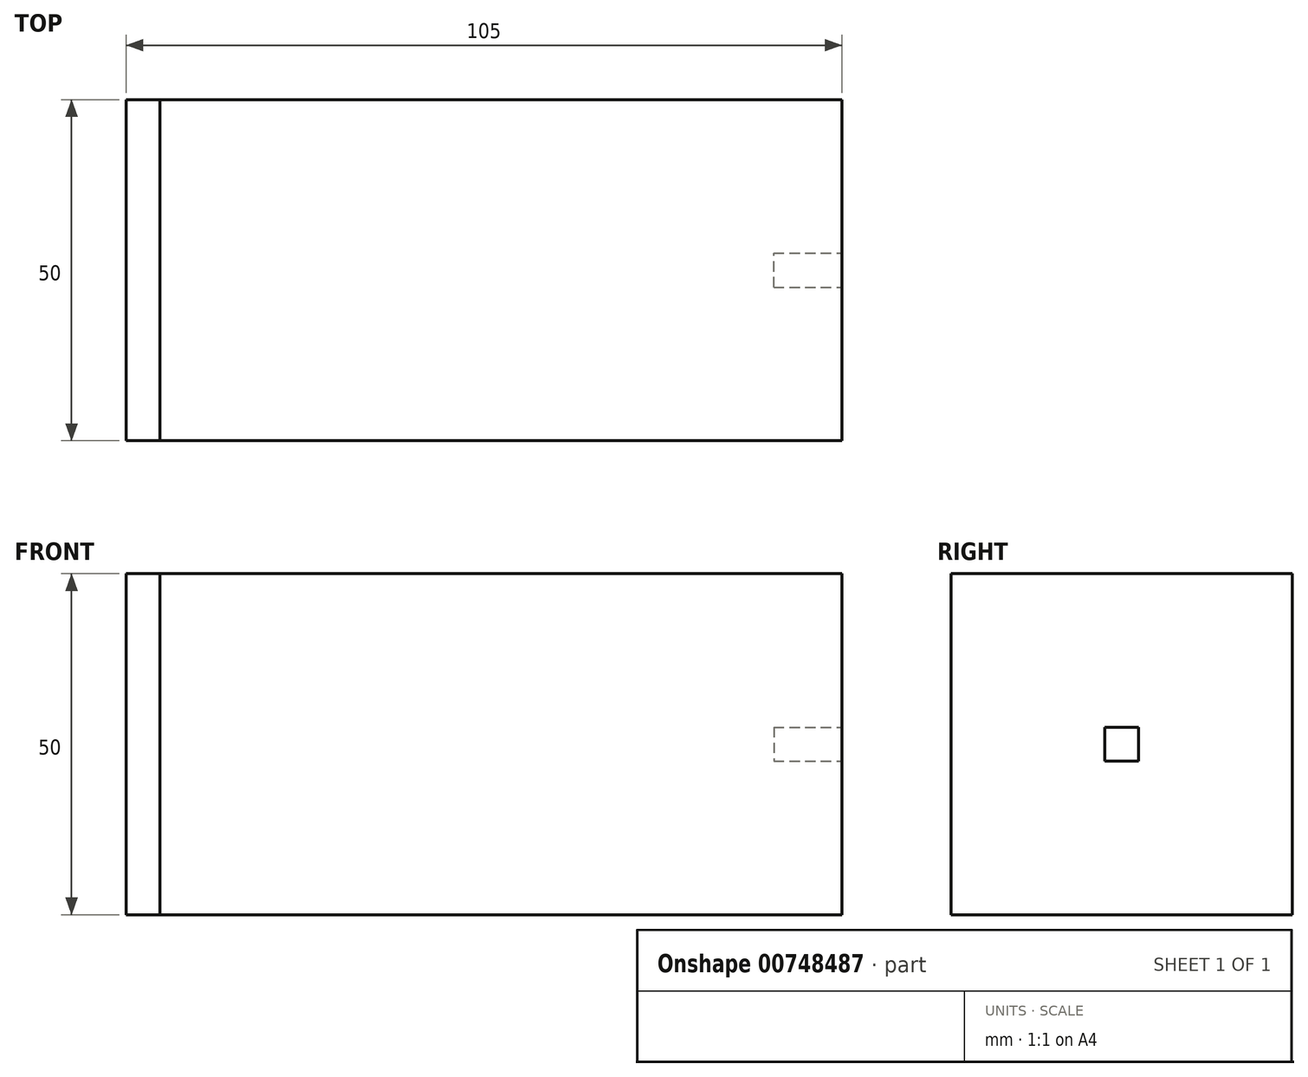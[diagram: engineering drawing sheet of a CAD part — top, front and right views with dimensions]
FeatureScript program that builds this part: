
annotation { "Feature Type Name" : "Feature", "Feature Type Description" : "" }
export const myFeature = defineFeature(function(context is Context, id is Id, definition is map)
    precondition{}
    {
        {
            var Q0;
            Q0=qCreatedBy(makeId("Front.planeOp"),FACE);
            var sketch = newSketch(context, id + "F0", { "sketchPlane" : qUnion([Q0])});
            skLineSegment(sketch, "E0.bottom", {"start": v(0, 0) * mm, "end": v(100, 0) * mm});
            skLineSegment(sketch, "E0.top", {"start": v(0, 50) * mm, "end": v(100, 50) * mm});
            skLineSegment(sketch, "E0.left", {"start": v(0, 0) * mm, "end": v(0, 50) * mm});
            skLineSegment(sketch, "E0.right", {"start": v(100, 0) * mm, "end": v(100, 50) * mm});
            skSolve(sketch);
        }
        {
            var Q0;
            Q0=qSketchRegion(id+"F0",true);
            extrude(context, id + "F1", {"entities" : qUnion([Q0]), "depth" : 50 * mm, "offsetDistance" : 25 * mm});
        }
        {
            var Q0;
            Q0=qCreatedBy(makeId("Right.planeOp"),FACE);
            var sketch = newSketch(context, id + "F2", { "sketchPlane" : qUnion([Q0])});
            skSolve(sketch);
        }
        {
            var Q0;
            Q0=makeQuery(id+"F1.opExtrude","SWEPT_FACE",FACE,{"disambiguationData":[OSD([sQuery(id+"F0.wireOp",EDGE,"E0.left")])]});
            var Q1;
            Q1=qSketchRegion(id+"F2",true);
            extrude(context, id + "F3", {"entities" : qUnion([Q0, Q1]), "depth" : 5 * mm, "offsetDistance" : 25 * mm});
        }
        {
            var Q0;
            Q0=makeQuery(id+"F1.opExtrude","SWEPT_FACE",FACE,{"disambiguationData":[OSD([sQuery(id+"F0.wireOp",EDGE,"E0.right")])]});
            var sketch = newSketch(context, id + "F4", { "sketchPlane" : qUnion([Q0])});
            skLineSegment(sketch, "E1.bottom", {"start": v(-27.5, 27.5) * mm, "end": v(-22.5, 27.5) * mm});
            skLineSegment(sketch, "E1.top", {"start": v(-27.5, 22.5) * mm, "end": v(-22.5, 22.5) * mm});
            skLineSegment(sketch, "E1.left", {"start": v(-27.5, 27.5) * mm, "end": v(-27.5, 22.5) * mm});
            skLineSegment(sketch, "E1.right", {"start": v(-22.5, 27.5) * mm, "end": v(-22.5, 22.5) * mm});
            skLineSegment(sketch, "E2", {"start": v(-25, 50) * mm, "end": v(-25, 0) * mm, "construction": true});
            skLineSegment(sketch, "E3", {"start": v(-50, 25) * mm, "end": v(0, 25) * mm, "construction": true});
            skSolve(sketch);
        }
        {
            var Q0;
            Q0=qSketchRegion(id+"F4",true);
            extrude(context, id + "F5", {"entities" : qUnion([Q0]), "oppositeDirection" : true, "depth" : 10 * mm, "offsetDistance" : 25 * mm});
        }
    });
